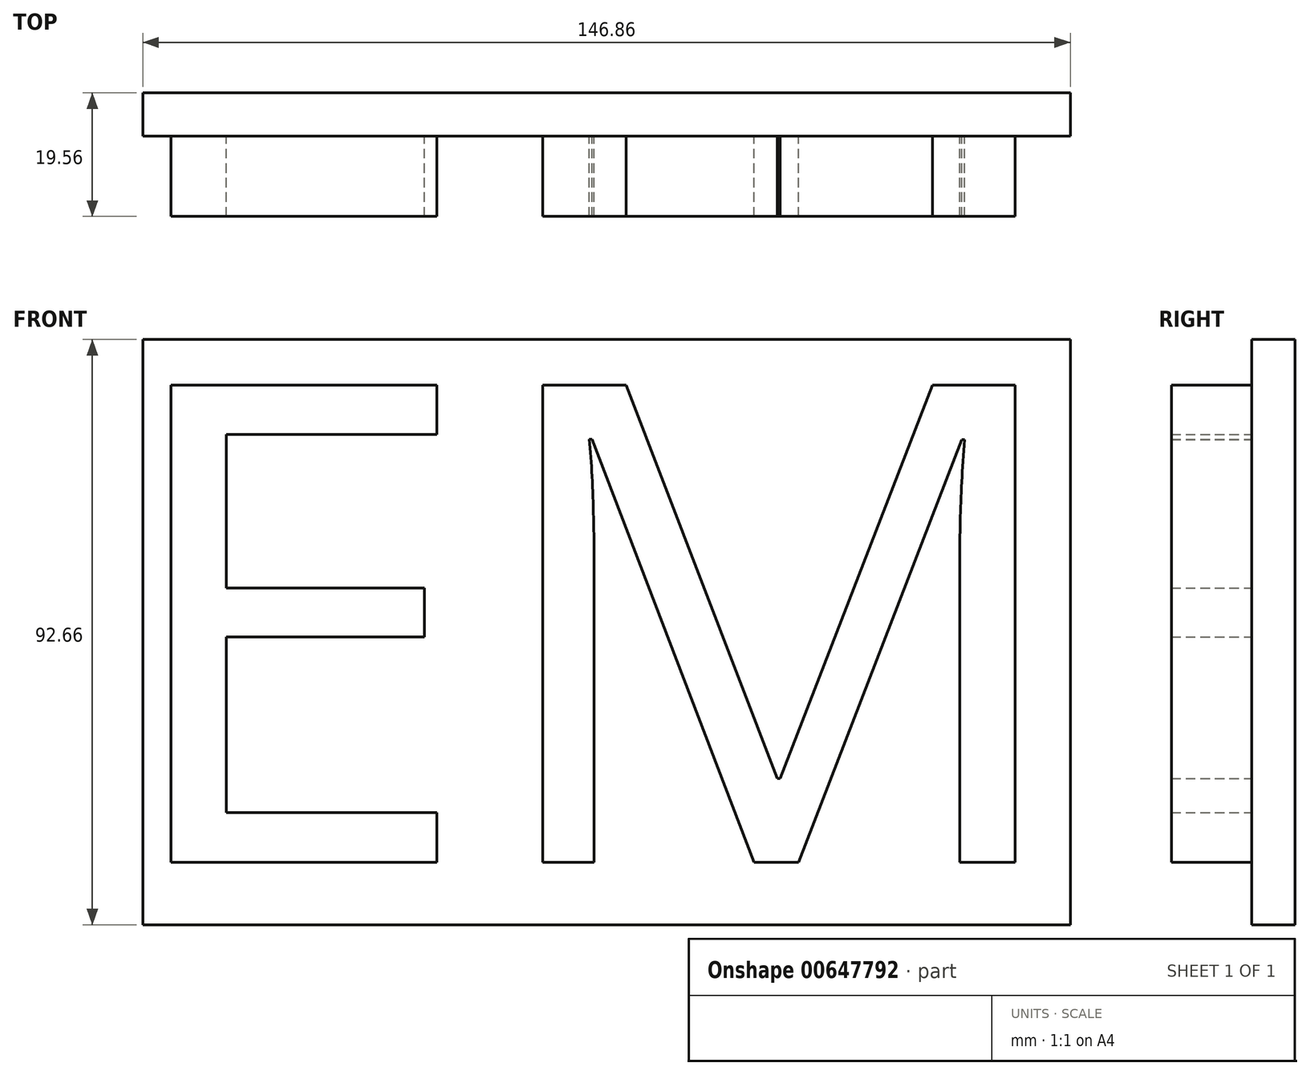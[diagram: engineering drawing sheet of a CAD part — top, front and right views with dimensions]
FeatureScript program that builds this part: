
annotation { "Feature Type Name" : "Feature", "Feature Type Description" : "" }
export const myFeature = defineFeature(function(context is Context, id is Id, definition is map)
    precondition{}
    {
        {
            var Q0;
            Q0=qCreatedBy(makeId("Front.planeOp"),FACE);
            var sketch = newSketch(context, id + "F0", { "sketchPlane" : qUnion([Q0])});
            skText(sketch, "E0", { "text": "EM", "fontName": "OpenSans-Regular.ttf"});
            const initialGuessF0  = {"E0": [-0.05118, -0.0423, 1, 0, 0.0762]};
            skSetInitialGuess(sketch, initialGuessF0);
            skSolve(sketch);
        }
        {
            var Q0;
            Q0 = qSketchRegion(id + "F0", true);
            extrude(context, id + "F1", {"entities" : qUnion([Q0]), "depth" : 12.7 * mm, "offsetDistance" : 25.4 * mm});
        }
        {
            var Q0;
            Q0=qCreatedBy(makeId("Front.planeOp"),FACE);
            var sketch = newSketch(context, id + "F2", { "sketchPlane" : qUnion([Q0])});
            skLineSegment(sketch, "E1.bottom", {"start": v(-45.26, 40.45) * mm, "end": v(101.6, 40.45) * mm});
            skLineSegment(sketch, "E1.top", {"start": v(-45.26, -52.21) * mm, "end": v(101.6, -52.21) * mm});
            skLineSegment(sketch, "E1.left", {"start": v(-45.26, 40.45) * mm, "end": v(-45.26, -52.21) * mm});
            skLineSegment(sketch, "E1.right", {"start": v(101.6, 40.45) * mm, "end": v(101.6, -52.21) * mm});
            skSolve(sketch);
        }
        {
            var Q0;
            Q0 = qSketchRegion(id + "F2", true);
            extrude(context, id + "F3", {"entities" : qUnion([Q0]), "operationType" : NewBodyOperationType.ADD, "oppositeDirection" : true, "depth" : 6.86 * mm, "offsetDistance" : 25.4 * mm});
        }
    });
